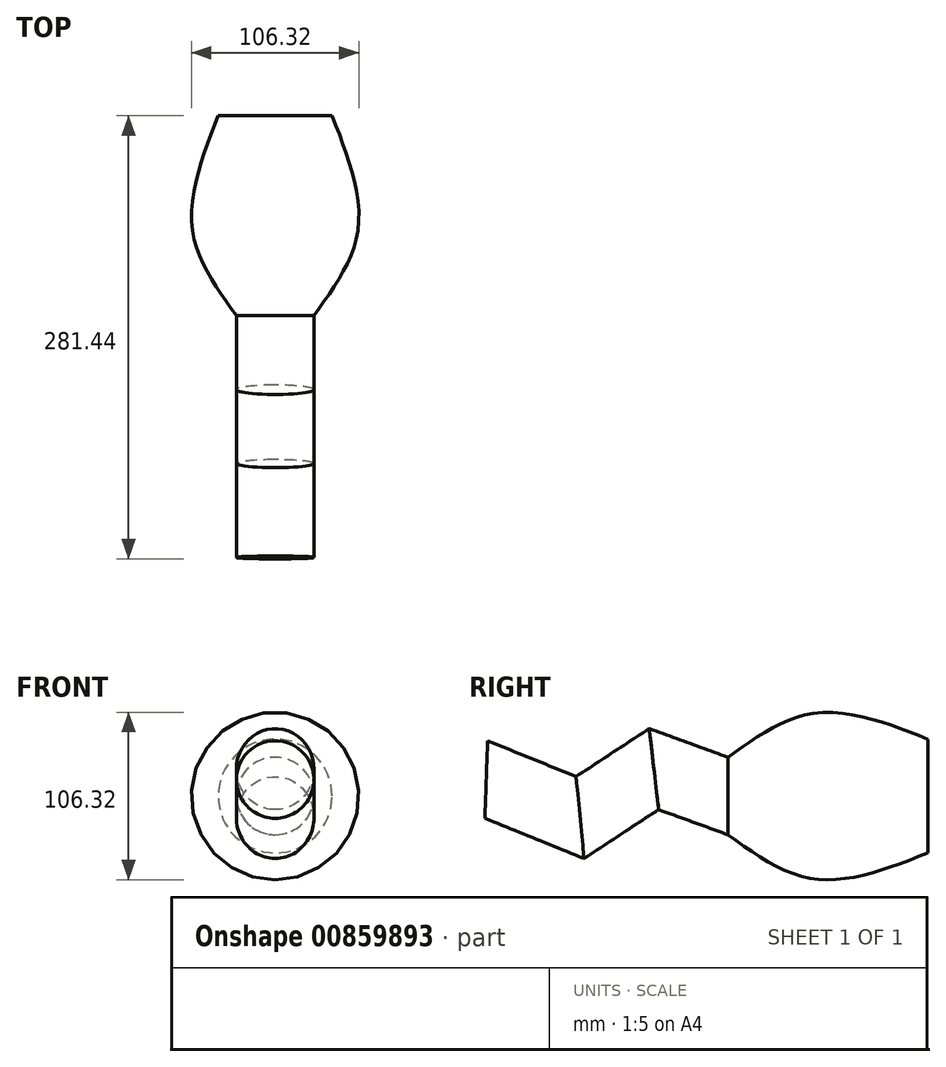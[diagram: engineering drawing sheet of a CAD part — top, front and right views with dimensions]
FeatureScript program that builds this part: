
annotation { "Feature Type Name" : "Feature", "Feature Type Description" : "" }
export const myFeature = defineFeature(function(context is Context, id is Id, definition is map)
    precondition{}
    {
        {
            var Q0;
            Q0=qCreatedBy(makeId("Front.planeOp"),FACE);
            var sketch = newSketch(context, id + "F0", { "sketchPlane" : qUnion([Q0])});
            skCircle(sketch, "E0", {"center": v(0, 0) * mm, "radius": 24.62 * mm});
            skSolve(sketch);
        }
        {
            var Q0;
            Q0=qCreatedBy(makeId("Right.planeOp"),FACE);
            var sketch = newSketch(context, id + "F1", { "sketchPlane" : qUnion([Q0])});
            skLineSegment(sketch, "E1", {"start": v(0, 0) * mm, "end": v(-47.06, 17.12) * mm});
            skLineSegment(sketch, "E2", {"start": v(-47.06, 17.12) * mm, "end": v(-93.97, -13.67) * mm});
            skLineSegment(sketch, "E3", {"start": v(-93.97, -13.67) * mm, "end": v(-153.54, 10.5) * mm});
            skSolve(sketch);
        }
        {
            var Q0;
            Q0=makeQuery(id+"F0.imprint","IMPRINT",FACE,{"disambiguationData":[TD([[makeQuery(id+"F0.imprint","IMPRINT",EDGE,{"derivedFrom":sQuery(id+"F0.wireOp",EDGE,"E0")}),1.0]])]});
            var Q1;
            Q1=sQuery(id+"F1.wireOp",EDGE,"E1");
            var Q2;
            Q2=sQuery(id+"F1.wireOp",EDGE,"E2");
            var Q3;
            Q3=sQuery(id+"F1.wireOp",EDGE,"E3");
            sweep(context, id + "F2", {"profiles" : qUnion([Q0]), "path" : qUnion([Q1, Q2, Q3])});
        }
        {
            var Q0;
            Q0=qCreatedBy(makeId("Front.planeOp"),FACE);
            cPlane(context, id + "F3", {"entities" : qUnion([Q0]), "cplaneType" : CPlaneType.OFFSET, "offset" : 50.8 * mm, "oppositeDirection" : true, "width" : 152.4 * mm, "height" : 152.4 * mm});
        }
        {
            var Q0;
            Q0=qCreatedBy(id+"F3.planeOp",FACE);
            cPlane(context, id + "F4", {"entities" : qUnion([Q0]), "cplaneType" : CPlaneType.OFFSET, "offset" : 76.2 * mm, "oppositeDirection" : true, "width" : 152.4 * mm, "height" : 152.4 * mm});
        }
        {
            var Q0;
            Q0=qCreatedBy(id+"F3.planeOp",FACE);
            var sketch = newSketch(context, id + "F5", { "sketchPlane" : qUnion([Q0])});
            skCircle(sketch, "E4", {"center": v(0, 0) * mm, "radius": 51.94 * mm});
            skSolve(sketch);
        }
        {
            var Q0;
            Q0=qCreatedBy(id+"F4.planeOp",FACE);
            var sketch = newSketch(context, id + "F6", { "sketchPlane" : qUnion([Q0])});
            skCircle(sketch, "E5", {"center": v(0, 0) * mm, "radius": 36.12 * mm});
            skSolve(sketch);
        }
        {
            var Q0;
            Q0=makeQuery(id+"F2.opSweep","CAP_FACE",FACE,{"disambiguationData":[OSD([sQuery(id+"F0.wireOp",EDGE,"E0"),sQuery(id+"F1.wireOp",VERTEX,"E1.start")])],"isStart":true});
            var Q1;
            Q1=makeQuery(id+"F5.imprint","IMPRINT",FACE,{"disambiguationData":[TD([[makeQuery(id+"F5.imprint","IMPRINT",EDGE,{"derivedFrom":sQuery(id+"F5.wireOp",EDGE,"E4")}),1.0]])]});
            var Q2;
            Q2=makeQuery(id+"F6.imprint","IMPRINT",FACE,{"disambiguationData":[TD([[makeQuery(id+"F6.imprint","IMPRINT",EDGE,{"derivedFrom":sQuery(id+"F6.wireOp",EDGE,"E5")}),1.0]])]});
            loft(context, id + "F7", {"sheetProfilesArray" : [{ "sheetProfileEntities" : qUnion([Q0]) }, { "sheetProfileEntities" : qUnion([Q1]) }, { "sheetProfileEntities" : qUnion([Q2]) }]});
        }
    });
